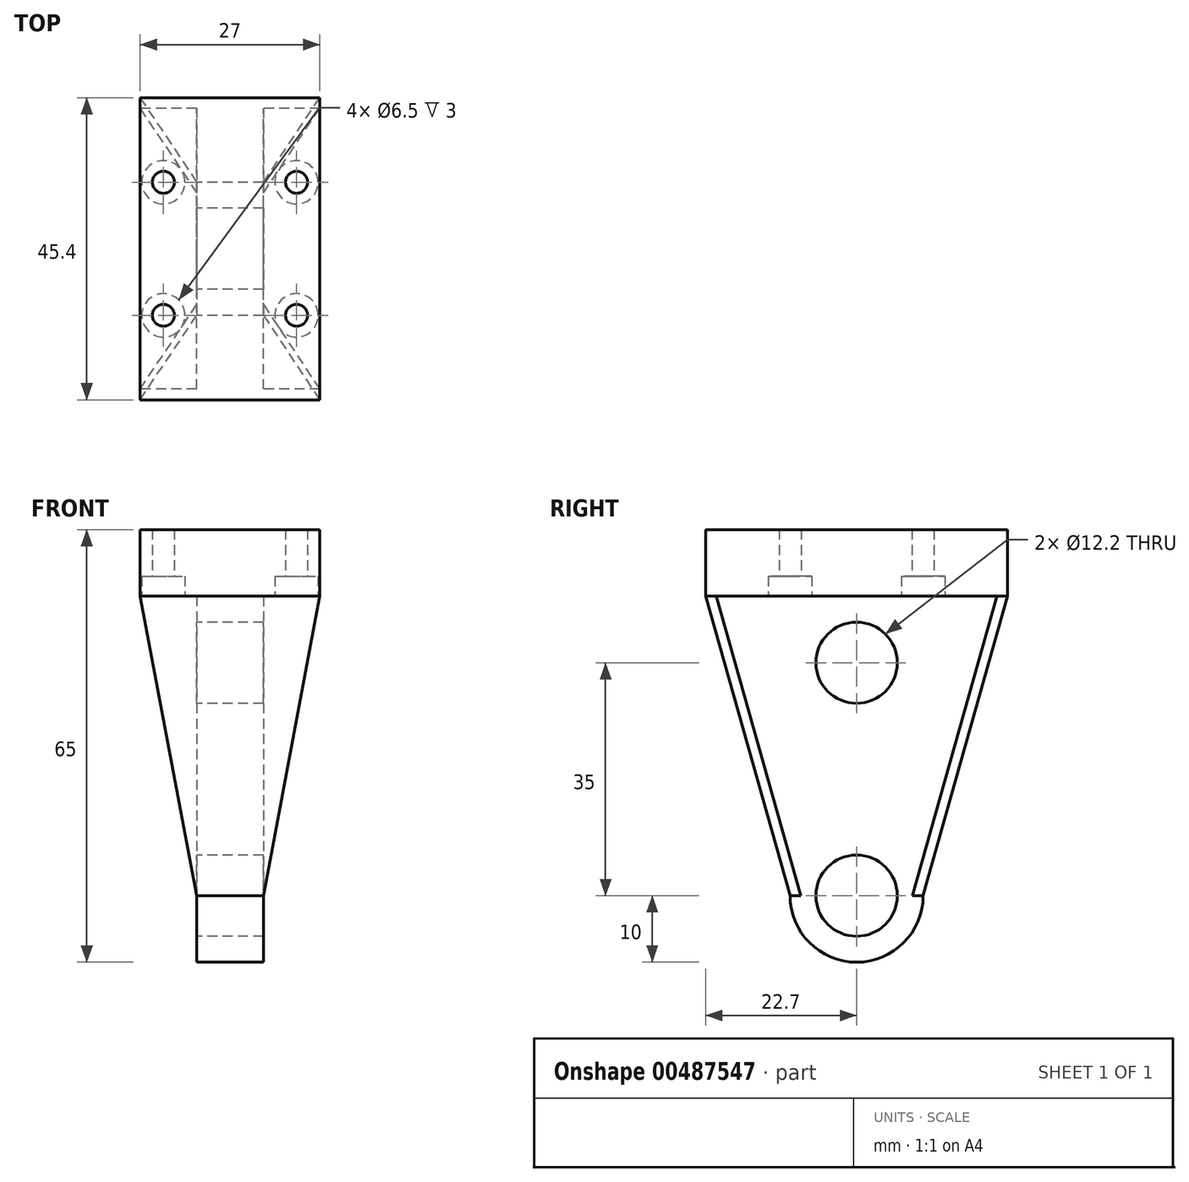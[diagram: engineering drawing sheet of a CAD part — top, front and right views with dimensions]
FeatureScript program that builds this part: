
annotation { "Feature Type Name" : "Feature", "Feature Type Description" : "" }
export const myFeature = defineFeature(function(context is Context, id is Id, definition is map)
    precondition{}
    {
        {
            var Q0;
            Q0=qCreatedBy(makeId("Right.planeOp"),FACE);
            var sketch = newSketch(context, id + "F0", { "sketchPlane" : qUnion([Q0])});
            skLineSegment(sketch, "E0", {"start": v(0, 0) * mm, "end": v(-22.7, 0) * mm});
            skCircle(sketch, "E1", {"center": v(0, -10) * mm, "radius": 6.1 * mm});
            skCircle(sketch, "E2", {"center": v(0, -45) * mm, "radius": 6.1 * mm});
            skCircle(sketch, "E3", {"center": v(0, -45) * mm, "radius": 10 * mm});
            skLineSegment(sketch, "E4", {"start": v(-10, -45) * mm, "end": v(-22.7, 0) * mm});
            skLineSegment(sketch, "E5", {"start": v(0, -45) * mm, "end": v(-10, -45) * mm, "construction": true});
            skLineSegment(sketch, "E6.MirrorCS", {"start": v(10, -45) * mm, "end": v(22.7, 0) * mm});
            skLineSegment(sketch, "E7.MirrorCS", {"start": v(0, 0) * mm, "end": v(22.7, 0) * mm});
            skSolve(sketch);
        }
        {
            var Q0;
            Q0=makeQuery(id+"F0.imprint","IMPRINT",FACE,{"disambiguationData":[TD([[makeQuery(id+"F0.imprint","IMPRINT",EDGE,{"derivedFrom":sQuery(id+"F0.wireOp",EDGE,"E0")}),1.0]])]});
            var Q1;
            Q1=makeQuery(id+"F0.imprint","IMPRINT",FACE,{"disambiguationData":[TD([[makeQuery(id+"F0.imprint","IMPRINT",EDGE,{"derivedFrom":sQuery(id+"F0.wireOp",EDGE,"E2")}),-1.0]])]});
            extrude(context, id + "F1", {"entities" : qUnion([Q0, Q1]), "depth" : 10 * mm, "offsetDistance" : 25 * mm});
        }
        {
            var Q0;
            Q0=makeQuery(id+"F1.opExtrude","SWEPT_FACE",FACE,{"disambiguationData":[OSD([sQuery(id+"F0.wireOp",EDGE,"E0"),sQuery(id+"F0.wireOp",EDGE,"E7.MirrorCS")])]});
            var sketch = newSketch(context, id + "F2", { "sketchPlane" : qUnion([Q0])});
            skLineSegment(sketch, "E8.bottom", {"start": v(18.5, -22.7) * mm, "end": v(-8.5, -22.7) * mm});
            skLineSegment(sketch, "E8.top", {"start": v(18.5, 22.7) * mm, "end": v(-8.5, 22.7) * mm});
            skLineSegment(sketch, "E8.left", {"start": v(18.5, -22.7) * mm, "end": v(18.5, 22.7) * mm});
            skLineSegment(sketch, "E8.right", {"start": v(-8.5, -22.7) * mm, "end": v(-8.5, 22.7) * mm});
            skPoint(sketch, "E8.middle", {"position": v(5, 0) * mm});
            skPoint(sketch, "E8.middle.positionSnap0", {"position": v(5, 22.7) * mm});
            skPoint(sketch, "E8.centerSnap0", {"position": v(5, 22.7) * mm});
            skSolve(sketch);
        }
        {
            var Q0;
            {var subQ2=sQuery(id+"F2.wireOp",EDGE,"E8.left");Q0=makeQuery(id+"F2.imprint","IMPRINT",FACE,{"disambiguationData":[TD([[makeQuery(id+"F2.imprint","IMPRINT",EDGE,{"derivedFrom":subQ2}),1.0]])]});}
            var Q1;
            {var subQ1=sQuery(id+"F0.wireOp",EDGE,"E7.MirrorCS");var subQ2=sQuery(id+"F0.wireOp",EDGE,"E0");var subQ3=makeQuery(id+"F1.opExtrude","CAP_EDGE",EDGE,{"disambiguationData":[OSD([subQ2,subQ1])],"isStart":true});Q1=makeQuery(id+"F2.imprint","IMPRINT",FACE,{"disambiguationData":[TD([[makeQuery(id+"F2.imprint","IMPRINT",EDGE,{"derivedFrom":subQ3}),-1.0]])]});}
            var Q2;
            {var subQ2=sQuery(id+"F2.wireOp",EDGE,"E8.right");Q2=makeQuery(id+"F2.imprint","IMPRINT",FACE,{"disambiguationData":[TD([[makeQuery(id+"F2.imprint","IMPRINT",EDGE,{"derivedFrom":subQ2}),-1.0]])]});}
            extrude(context, id + "F3", {"entities" : qUnion([Q0, Q1, Q2]), "operationType" : NewBodyOperationType.ADD, "depth" : 10 * mm, "offsetDistance" : 25 * mm});
        }
        {
            var Q0;
            {var subQ0=sQuery(id+"F2.wireOp",EDGE,"E8.bottom");var subQ3=sQuery(id+"F2.wireOp",EDGE,"E8.right");var subQ4=sQuery(id+"F2.wireOp",EDGE,"E8.top");Q0=makeQuery(id+"F3.boolean.opBoolean","SPLIT",FACE,{"disambiguationData":[TD([makeQuery(id+"F3.opExtrude","SWEPT_FACE",FACE,{"disambiguationData":[OSD([subQ3])]})])],"derivedFrom":makeQuery(id+"F3.opExtrude","CAP_FACE",FACE,{"disambiguationData":[OSD([subQ0,subQ4,sQuery(id+"F2.wireOp",EDGE,"E8.left"),subQ3])],"isStart":true})});}
            var sketch = newSketch(context, id + "F4", { "sketchPlane" : qUnion([Q0])});
            skLineSegment(sketch, "E9", {"start": v(5, 22.7) * mm, "end": v(5, -22.7) * mm, "construction": true});
            skLineSegment(sketch, "E10", {"start": v(-8.5, 0) * mm, "end": v(18.5, 0) * mm, "construction": true});
            skPoint(sketch, "E11", {"position": v(-5, 10) * mm});
            skPoint(sketch, "E12.MirrorP", {"position": v(15, 10) * mm});
            skPoint(sketch, "E13.MirrorP", {"position": v(15, -10) * mm});
            skPoint(sketch, "E14.MirrorP", {"position": v(-5, -10) * mm});
            skLineSegment(sketch, "E15.bottom", {"start": v(-8.5, 22.7) * mm, "end": v(0, 22.7) * mm});
            skLineSegment(sketch, "E15.top", {"start": v(-8.5, 17.7) * mm, "end": v(0, 17.7) * mm});
            skLineSegment(sketch, "E15.left", {"start": v(-8.5, 22.7) * mm, "end": v(-8.5, 17.7) * mm});
            skLineSegment(sketch, "E15.right", {"start": v(0, 22.7) * mm, "end": v(0, 17.7) * mm});
            skLineSegment(sketch, "E16.MirrorCS", {"start": v(18.5, 17.7) * mm, "end": v(10, 17.7) * mm});
            skLineSegment(sketch, "E17.MirrorCS", {"start": v(18.5, 22.7) * mm, "end": v(10, 22.7) * mm});
            skLineSegment(sketch, "E18.MirrorCS", {"start": v(18.5, 22.7) * mm, "end": v(18.5, 17.7) * mm});
            skLineSegment(sketch, "E19.MirrorCS", {"start": v(10, 22.7) * mm, "end": v(10, 17.7) * mm});
            skLineSegment(sketch, "E20.MirrorCS", {"start": v(-8.5, -17.7) * mm, "end": v(0, -17.7) * mm});
            skLineSegment(sketch, "E21.MirrorCS", {"start": v(18.5, -17.7) * mm, "end": v(10, -17.7) * mm});
            skLineSegment(sketch, "E22.MirrorCS", {"start": v(10, -22.7) * mm, "end": v(10, -17.7) * mm});
            skLineSegment(sketch, "E23.MirrorCS", {"start": v(0, -22.7) * mm, "end": v(0, -17.7) * mm});
            skLineSegment(sketch, "E24.MirrorCS", {"start": v(-8.5, -22.7) * mm, "end": v(-8.5, -17.7) * mm});
            skLineSegment(sketch, "E25.MirrorCS", {"start": v(-8.5, -22.7) * mm, "end": v(0, -22.7) * mm});
            skLineSegment(sketch, "E26.MirrorCS", {"start": v(18.5, -22.7) * mm, "end": v(10, -22.7) * mm});
            skLineSegment(sketch, "E27.MirrorCS", {"start": v(18.5, -22.7) * mm, "end": v(18.5, -17.7) * mm});
            skSolve(sketch);
        }
        {
            var Q0;
            Q0=sQuery(id+"F4.wireOp",VERTEX,"E11");
            var Q1;
            Q1=sQuery(id+"F4.wireOp",VERTEX,"E12.MirrorP");
            var Q2;
            Q2=sQuery(id+"F4.wireOp",VERTEX,"E13.MirrorP");
            var Q3;
            Q3=sQuery(id+"F4.wireOp",VERTEX,"E14.MirrorP");
            var Q4;
            Q4=makeQuery(id+"F1.opExtrude","SWEPT_BODY",BODY,{"disambiguationData":[OSD([sQuery(id+"F0.wireOp",EDGE,"E0"),sQuery(id+"F0.wireOp",EDGE,"E1"),sQuery(id+"F0.wireOp",EDGE,"E2"),sQuery(id+"F0.wireOp",EDGE,"E3"),sQuery(id+"F0.wireOp",EDGE,"E4"),sQuery(id+"F0.wireOp",EDGE,"E6.MirrorCS"),sQuery(id+"F0.wireOp",EDGE,"E7.MirrorCS")])]});
            hole(context, id + "F5", {"style" : HoleStyle.C_BORE, "endStyle" : HoleEndStyle.THROUGH, "standardTappedOrClearance" : lookupTablePath({ "standard" : "ISO", "fit" : "Normal", "size" : "M3", "type" : "Clearance" }), "standardBlindInLast" : lookupTablePath({ "fit" : "Standard", "standard" : "ISO", "size" : "M3", "type" : "Clearance" }), "holeDiameter" : 3.3 * mm, "cBoreDiameter" : 6.5 * mm, "cBoreDepth" : 3 * mm, "isTappedThrough" : true, "tappedDepth" : 12 * mm, "tapClearance" : 3, "locations" : qUnion([Q0, Q1, Q2, Q3]), "scope" : qUnion([Q4])});
        }
        {
            var Q0;
            Q0=makeQuery(id+"F1.opExtrude","CAP_FACE",FACE,{"disambiguationData":[OSD([sQuery(id+"F0.wireOp",EDGE,"E0"),sQuery(id+"F0.wireOp",EDGE,"E1"),sQuery(id+"F0.wireOp",EDGE,"E2"),sQuery(id+"F0.wireOp",EDGE,"E3"),sQuery(id+"F0.wireOp",EDGE,"E4"),sQuery(id+"F0.wireOp",EDGE,"E6.MirrorCS"),sQuery(id+"F0.wireOp",EDGE,"E7.MirrorCS")])],"isStart":false});
            var sketch = newSketch(context, id + "F6", { "sketchPlane" : qUnion([Q0])});
            skCircle(sketch, "E28", {"center": v(0, -45) * mm, "radius": 8.4 * mm});
            skLineSegment(sketch, "E29", {"start": v(-8.4, -45) * mm, "end": v(0, -45) * mm, "construction": true});
            skLineSegment(sketch, "E30", {"start": v(-8.4, -45) * mm, "end": v(-21.1, 0) * mm});
            skLineSegment(sketch, "E31.MirrorCS", {"start": v(8.4, -45) * mm, "end": v(21.1, 0) * mm});
            skSolve(sketch);
        }
        {
            var Q0;
            {var subQ1=sQuery(id+"F6.wireOp",EDGE,"E30");Q0=makeQuery(id+"F6.imprint","IMPRINT",FACE,{"disambiguationData":[TD([[makeQuery(id+"F6.imprint","IMPRINT",EDGE,{"derivedFrom":subQ1}),1.0]])]});}
            extrude(context, id + "F7", {"entities" : qUnion([Q0]), "operationType" : NewBodyOperationType.ADD, "depth" : 8.5 * mm, "offsetDistance" : 25 * mm, "hasSecondDirection" : true, "secondDirectionOppositeDirection" : true, "secondDirectionDepth" : 18.5 * mm});
        }
        {
            var Q0;
            Q0=makeQuery(id+"F3.opExtrude","SWEPT_FACE",FACE,{"disambiguationData":[OSD([sQuery(id+"F2.wireOp",EDGE,"E8.bottom")])]});
            var sketch = newSketch(context, id + "F8", { "sketchPlane" : qUnion([Q0])});
            skLineSegment(sketch, "E32", {"start": v(-8.5, 0) * mm, "end": v(0, -45) * mm});
            skLineSegment(sketch, "E33", {"start": v(0, -45) * mm, "end": v(0, -55) * mm});
            skLineSegment(sketch, "E34", {"start": v(0, -55) * mm, "end": v(10, -55) * mm});
            skLineSegment(sketch, "E35", {"start": v(10, -55) * mm, "end": v(10, -45) * mm});
            skLineSegment(sketch, "E36", {"start": v(10, -45) * mm, "end": v(18.5, 0) * mm});
            skLineSegment(sketch, "E37", {"start": v(18.5, 0) * mm, "end": v(18.5, -58.93) * mm});
            skLineSegment(sketch, "E38", {"start": v(18.5, -58.93) * mm, "end": v(-8.5, -58.93) * mm});
            skLineSegment(sketch, "E39", {"start": v(-8.5, -58.93) * mm, "end": v(-8.5, 0) * mm});
            skLineSegment(sketch, "E40", {"start": v(-8.5, -45) * mm, "end": v(18.5, -45) * mm, "construction": true});
            skLineSegment(sketch, "E41", {"start": v(-8.5, -55) * mm, "end": v(18.5, -55) * mm, "construction": true});
            skLineSegment(sketch, "E42", {"start": v(5, 10) * mm, "end": v(5, -55) * mm, "construction": true});
            skSolve(sketch);
        }
        {
            var Q0;
            Q0=makeQuery(id+"F8.imprint","IMPRINT",FACE,{"disambiguationData":[TD([[makeQuery(id+"F8.imprint","IMPRINT",EDGE,{"derivedFrom":sQuery(id+"F8.wireOp",EDGE,"E32")}),-1.0]])]});
            extrude(context, id + "F9", {"entities" : qUnion([Q0]), "operationType" : NewBodyOperationType.REMOVE, "endBound" : BoundingType.THROUGH_ALL, "oppositeDirection" : true, "depth" : 25 * mm, "offsetDistance" : 25 * mm});
        }
    });
